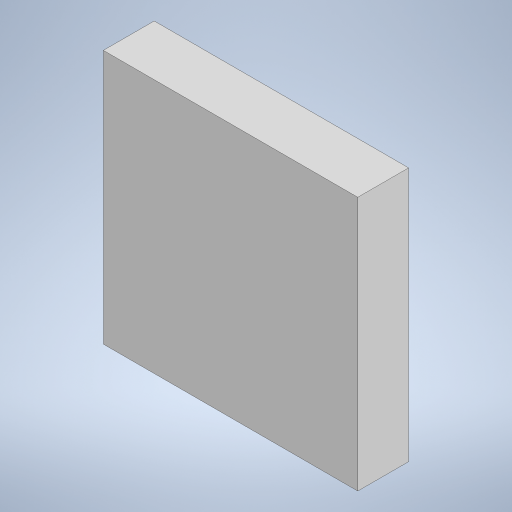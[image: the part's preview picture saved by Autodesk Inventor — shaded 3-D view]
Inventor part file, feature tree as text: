
AUTODESK INVENTOR PART (.ipt)
format: ipt  version: 2023 (Build 270158000, 158)  size: 183,296 bytes
history: native  units: in
note: dims shown in document units (in); Inventor stores cm internally (conversion verified against a paired STEP export)
features: extrude x1, sketch x1
ambient origin geometry x8: Origin, YZ Plane, XZ Plane, XY Plane, X Axis, Y Axis, Z Axis, Center Point
bodies: Solid1 (feature_tree)
feature tree (2):
  extrude  "Extrusion1"  Depth=0.3937in
  sketch  "Sketch1"  dims[d0=0.3937in d1=0.3937in d2=0.0787in d3=0.0in]
